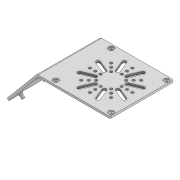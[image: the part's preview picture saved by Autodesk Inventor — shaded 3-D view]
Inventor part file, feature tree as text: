
AUTODESK INVENTOR PART (.ipt)
format: ipt  version: 2020 (Build 240168000, 168)  size: 429,568 bytes
history: native  units: mm
features: sketch x14, extrude x13, pattern_circular x2, chamfer x2, fillet x2, pattern_linear x1, plane x1
ambient origin geometry x8: Origin, YZ Plane, XZ Plane, XY Plane, X Axis, Y Axis, Z Axis, Center Point
bodies: Solid1 (feature_tree)
feature tree (35):
  extrude  "Extrusion1"  Depth=104.5mm
  extrude  "Extrusion2"  Depth=120.0mm
  extrude  "Extrusion3"  Depth=4.0mm
  pattern_linear  "Rectangular Pattern1"  Count1=10  [1 undecoded]
  pattern_circular  "Circular Pattern1"  Count=5  [1 undecoded]
  extrude  "Extrusion4"  TaperAngle=22.5deg  [1 undecoded]
  pattern_circular  "Circular Pattern2"  Count=8 Angle=360.0deg
  plane  "Work Plane1"
  extrude  "Extrusion5"  Depth=4.0mm
  extrude  "Extrusion6"  Depth=4.0mm TaperAngle=0.0deg
  extrude  "Extrusion7"  Depth=4.0mm
  chamfer  "Chamfer1"  Distance=90.0mm
  fillet  "Fillet1"  Radius=3.0mm
  extrude  "Extrusion8"  Depth=3.0mm
  sketch  "Sketch9"  dims[d14=5.0mm]
  extrude  "Extrusion9"  Depth=3.0mm
  fillet  "Fillet2"  Radius=3.0mm
  extrude  "Extrusion10"  Depth=4.0mm TaperAngle=0.0deg
  chamfer  "Chamfer2"  Distance=42.5mm
  extrude  "Extrusion11"  Depth=4.0mm
  extrude  "Extrusion12"  Depth=4.0mm
  extrude  "Extrusion13"  Depth=4.0mm
  sketch  "Sketch1"  dims[d0=104.5mm d1=104.5mm]
  sketch  "Sketch2"  dims[d2=160.0mm d3=120.0mm]
  sketch  "Sketch3"  dims[d4=4.0mm d5=4.0mm]
  sketch  "Sketch4"  dims[d6=4.0mm]
  sketch  "Sketch5"  dims[d7=4.0mm]
  sketch  "Sketch6"  dims[d8=4.0mm d9=0.0mm]
  sketch  "Sketch7"  dims[d10=4.0mm d11=100.0mm]
  sketch  "Sketch8"  dims[d12=4.0mm d13=0.0mm]
  sketch  "Sketch10"  dims[d15=4.0mm d16=0.0mm d17=50.0mm d19=10.0mm]
  sketch  "Sketch11"  dims[d20=80.0mm d21=360.0deg d23=22.5deg]
  sketch  "Sketch12"  dims[d24=32.0mm]
  sketch  "Sketch13"  dims[d25=4.0mm d26=0.0mm d27=80.0mm d28=360.0deg]
  sketch  "Sketch14"  dims[d30=40.142573mm d31=90.0mm d32=4.0mm d33=0.0mm d34=65.0mm d35=90.0mm d36=3.0mm d37=3.0mm d38=3.0mm d39=3.0mm d40=4.0mm d41=0.0mm d42=42.5mm d43=16.5mm d44=14.0mm d45=28.0mm d46=13.8mm d47=6.8mm d48=10.0mm d49=18.5mm d50=12.0mm d51=23.0mm d52=17.0mm d54=3.0mm d55=4.0mm d56=0.0mm d57=2.0mm d58=2.0mm d59=45.0deg d60=0.5mm d61=18.0mm d62=4.0mm d63=0.0mm d64=8.0mm d65=8.0mm d66=8.0mm d67=8.0mm d68=6.0mm d69=6.0mm d70=6.0mm d71=6.0mm d72=8.0mm d73=0.0mm d74=2.0mm d75=120.0mm d76=22.0mm d77=12.0mm d78=0.0mm d79=2.0mm d80=2.0mm d81=45.0deg d82=10.0mm d83=10.0mm d84=10.0mm d85=10.0mm d86=2.0mm d87=0.0mm d88=3.0mm d89=30.0mm d90=4.0mm d91=0.0mm d92=4.0mm d93=0.0mm d94=7.0mm]
note: 3 required parameter values undecoded (feature->parameter linkage not recoverable at this tier; creation-order binding heuristic only, values carry confidence <= 0.55)
